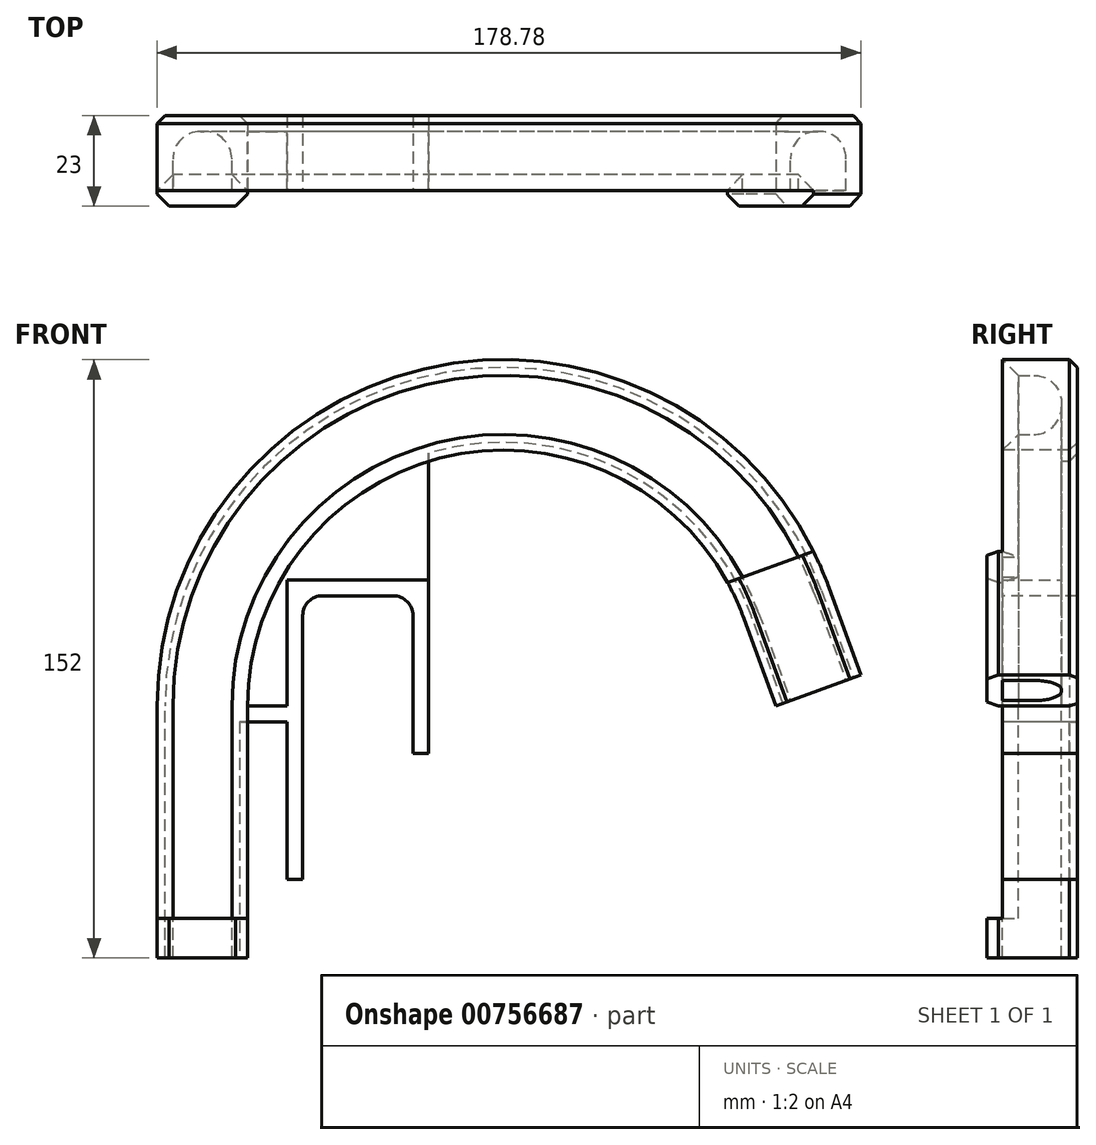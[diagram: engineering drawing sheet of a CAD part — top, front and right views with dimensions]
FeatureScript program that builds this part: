
annotation { "Feature Type Name" : "Feature", "Feature Type Description" : "" }
export const myFeature = defineFeature(function(context is Context, id is Id, definition is map)
    precondition{}
    {
        {
            var Q0;
            Q0=qCreatedBy(makeId("Front.planeOp"),FACE);
            var sketch = newSketch(context, id + "F0", { "sketchPlane" : qUnion([Q0])});
            skLineSegment(sketch, "E0.top", {"start": v(0, 60) * mm, "end": v(10, 60) * mm});
            skLineSegment(sketch, "E0.left", {"start": v(0, 0) * mm, "end": v(0, 60) * mm});
            skLineSegment(sketch, "E0.right", {"start": v(10, 20) * mm, "end": v(10, 60) * mm});
            skLineSegment(sketch, "E1.0", {"start": v(14, 20) * mm, "end": v(14, 64) * mm});
            skLineSegment(sketch, "E1.1", {"start": v(-4, 64) * mm, "end": v(14, 64) * mm});
            skLineSegment(sketch, "E1.2", {"start": v(-4, 0) * mm, "end": v(-4, 64) * mm});
            skLineSegment(sketch, "E2", {"start": v(10, 20) * mm, "end": v(14, 20) * mm});
            skLineSegment(sketch, "E3", {"start": v(-4, 0) * mm, "end": v(0, 0) * mm});
            skCircle(sketch, "E4", {"center": v(65, 64) * mm, "radius": 69 * mm, "construction": true});
            skLineSegment(sketch, "E5", {"start": v(65, 64) * mm, "end": v(129.84, 87.6) * mm, "construction": true});
            skArc(sketch, "E6", {"start": v(129.84, 87.6) * mm, "mid": v(53.02, 131.95) * mm, "end": v(-4, 64) * mm});
            skArc(sketch, "E7.0", {"start": v(126.08, 86.23) * mm, "mid": v(53.71, 128.01) * mm, "end": v(0, 64) * mm});
            skLineSegment(sketch, "E8", {"start": v(126.08, 86.23) * mm, "end": v(129.84, 87.6) * mm});
            skLineSegment(sketch, "E9.0", {"start": v(-19, 0) * mm, "end": v(-19, 64) * mm});
            skArc(sketch, "E9.1", {"start": v(143.93, 92.73) * mm, "mid": v(50.41, 146.72) * mm, "end": v(-19, 64) * mm});
            skLineSegment(sketch, "E10", {"start": v(-19, 0) * mm, "end": v(-4, 0) * mm});
            skLineSegment(sketch, "E11", {"start": v(143.93, 92.73) * mm, "end": v(129.84, 87.6) * mm});
            skLineSegment(sketch, "E12.0", {"start": v(-23, 0) * mm, "end": v(-23, 64) * mm});
            skArc(sketch, "E12.1", {"start": v(147.7, 94.1) * mm, "mid": v(49.72, 150.66) * mm, "end": v(-23, 64) * mm});
            skLineSegment(sketch, "E13", {"start": v(-23, 0) * mm, "end": v(-19, 0) * mm});
            skLineSegment(sketch, "E14", {"start": v(147.7, 94.1) * mm, "end": v(143.93, 92.73) * mm});
            skLineSegment(sketch, "E15", {"start": v(147.7, 94.1) * mm, "end": v(155.78, 71.87) * mm});
            skLineSegment(sketch, "E16", {"start": v(126.08, 86.23) * mm, "end": v(134.17, 64) * mm});
            skLineSegment(sketch, "E17", {"start": v(129.84, 87.6) * mm, "end": v(137.93, 65.37) * mm});
            skLineSegment(sketch, "E18", {"start": v(143.93, 92.73) * mm, "end": v(152.03, 70.5) * mm});
            skLineSegment(sketch, "E19", {"start": v(155.78, 71.87) * mm, "end": v(152.03, 70.5) * mm});
            skLineSegment(sketch, "E20", {"start": v(152.03, 70.5) * mm, "end": v(137.93, 65.37) * mm});
            skLineSegment(sketch, "E21", {"start": v(137.93, 65.37) * mm, "end": v(134.17, 64) * mm});
            skLineSegment(sketch, "E22", {"start": v(42, 52) * mm, "end": v(46, 52) * mm});
            skLineSegment(sketch, "E23", {"start": v(10, 64) * mm, "end": v(10, 92) * mm});
            skLineSegment(sketch, "E24", {"start": v(14, 92) * mm, "end": v(14, 64) * mm});
            skLineSegment(sketch, "E25", {"start": v(42, 92) * mm, "end": v(42, 52) * mm});
            skLineSegment(sketch, "E26", {"start": v(46, 52) * mm, "end": v(46, 92) * mm});
            skLineSegment(sketch, "E27", {"start": v(46, 92) * mm, "end": v(46, 128.01) * mm});
            skPoint(sketch, "E27.endSnap0", {"position": v(53.71, 128.01) * mm});
            skLineSegment(sketch, "E28", {"start": v(14, 92) * mm, "end": v(42, 92) * mm});
            skLineSegment(sketch, "E29", {"start": v(46, 96) * mm, "end": v(10, 96) * mm});
            skLineSegment(sketch, "E30", {"start": v(10, 96) * mm, "end": v(10, 92) * mm});
            skSolve(sketch);
        }
        {
            var Q0;
            Q0=qSketchRegion(id+"F0",true);
            extrude(context, id + "F1", {"entities" : qUnion([Q0]), "oppositeDirection" : true, "depth" : 4 * mm, "offsetDistance" : 25 * mm});
        }
        {
            var Q0;
            Q0=makeQuery(id+"F0.imprint","IMPRINT",FACE,{"disambiguationData":[TD([[makeQuery(id+"F0.imprint","IMPRINT",EDGE,{"derivedFrom":sQuery(id+"F0.wireOp",EDGE,"E0.top")}),1.0]])]});
            var Q1;
            {var subQ0=sQuery(id+"F0.wireOp",EDGE,"E6");Q1=makeQuery(id+"F0.imprint","IMPRINT",FACE,{"disambiguationData":[TD([[makeQuery(id+"F0.imprint","IMPRINT",EDGE,{"derivedFrom":subQ0}),1.0]])]});}
            var Q2;
            Q2=makeQuery(id+"F0.imprint","IMPRINT",FACE,{"disambiguationData":[TD([[makeQuery(id+"F0.imprint","IMPRINT",EDGE,{"derivedFrom":sQuery(id+"F0.wireOp",EDGE,"E9.0")}),1.0]])]});
            var Q3;
            Q3=makeQuery(id+"F0.imprint","IMPRINT",FACE,{"disambiguationData":[TD([[makeQuery(id+"F0.imprint","IMPRINT",EDGE,{"derivedFrom":sQuery(id+"F0.wireOp",EDGE,"E14")}),1.0]])]});
            var Q4;
            Q4=makeQuery(id+"F0.imprint","IMPRINT",FACE,{"disambiguationData":[TD([[makeQuery(id+"F0.imprint","IMPRINT",EDGE,{"derivedFrom":sQuery(id+"F0.wireOp",EDGE,"E8")}),-1.0]])]});
            var Q5;
            Q5=makeQuery(id+"F0.imprint","IMPRINT",FACE,{"disambiguationData":[TD([[makeQuery(id+"F0.imprint","IMPRINT",EDGE,{"derivedFrom":sQuery(id+"F0.wireOp",EDGE,"E22")}),1.0]])]});
            extrude(context, id + "F2", {"entities" : qUnion([Q0, Q1, Q2, Q3, Q4, Q5]), "operationType" : NewBodyOperationType.ADD, "depth" : 15 * mm, "offsetDistance" : 25 * mm});
        }
        {
            var Q0;
            Q0=makeQuery(id+"F2.opExtrude","CAP_EDGE",EDGE,{"disambiguationData":[OSD([sQuery(id+"F0.wireOp",EDGE,"E9.1")])],"isStart":true});
            var Q1;
            Q1=makeQuery(id+"F2.opExtrude","CAP_EDGE",EDGE,{"disambiguationData":[OSD([sQuery(id+"F0.wireOp",EDGE,"E6")])],"isStart":true});
            fillet(context, id + "F3", {"entities" : qUnion([Q0, Q1]), "radius" : 7 * mm, "tangentPropagation" : true, "allowEdgeOverflow" : false});
        }
        {
            var Q0;
            Q0=makeQuery(id+"F1.opExtrude","CAP_EDGE",EDGE,{"disambiguationData":[OSD([sQuery(id+"F0.wireOp",EDGE,"E16")])],"isStart":false});
            var Q1;
            Q1=makeQuery(id+"F1.opExtrude","CAP_EDGE",EDGE,{"disambiguationData":[OSD([sQuery(id+"F0.wireOp",EDGE,"E15")])],"isStart":false});
            var Q2;
            Q2=makeQuery(id+"F1.opExtrude","CAP_EDGE",EDGE,{"disambiguationData":[OSD([sQuery(id+"F0.wireOp",EDGE,"E0.left")])],"isStart":false});
            chamfer(context, id + "F4", {"entities" : qUnion([Q0, Q1, Q2]), "width" : 2 * mm, "tangentPropagation" : true});
        }
        {
            var Q0;
            Q0=makeQuery(id+"F2.opExtrude","CAP_FACE",FACE,{"disambiguationData":[OSD([sQuery(id+"F0.wireOp",EDGE,"E0.top"),sQuery(id+"F0.wireOp",EDGE,"E0.left"),sQuery(id+"F0.wireOp",EDGE,"E0.right"),sQuery(id+"F0.wireOp",EDGE,"E1.0"),sQuery(id+"F0.wireOp",EDGE,"E1.1"),sQuery(id+"F0.wireOp",EDGE,"E1.2"),sQuery(id+"F0.wireOp",EDGE,"E2"),sQuery(id+"F0.wireOp",EDGE,"E3"),sQuery(id+"F0.wireOp",EDGE,"E6"),sQuery(id+"F0.wireOp",EDGE,"E7.0"),sQuery(id+"F0.wireOp",EDGE,"E8")])],"isStart":false});
            var sketch = newSketch(context, id + "F5", { "sketchPlane" : qUnion([Q0])});
            skLineSegment(sketch, "E31.bottom", {"start": v(0, 0) * mm, "end": v(-23, 0) * mm});
            skLineSegment(sketch, "E31.top", {"start": v(0, 10) * mm, "end": v(-23, 10) * mm});
            skLineSegment(sketch, "E31.left", {"start": v(0, 0) * mm, "end": v(0, 10) * mm});
            skLineSegment(sketch, "E31.right", {"start": v(-23, 0) * mm, "end": v(-23, 10) * mm});
            skLineSegment(sketch, "E32", {"start": v(126.08, 86.23) * mm, "end": v(147.7, 94.1) * mm});
            skLineSegment(sketch, "E33", {"start": v(1.23, 51.43) * mm, "end": v(143.74, 103.3) * mm});
            skArc(sketch, "E34", {"start": v(126.08, 86.23) * mm, "mid": v(47.55, 126.61) * mm, "end": v(1.23, 51.43) * mm});
            skArc(sketch, "E35", {"start": v(147.7, 94.1) * mm, "mid": v(145.85, 98.76) * mm, "end": v(143.74, 103.3) * mm});
            skLineSegment(sketch, "E36", {"start": v(126.08, 86.23) * mm, "end": v(134.17, 64) * mm});
            skLineSegment(sketch, "E37", {"start": v(134.17, 64) * mm, "end": v(155.78, 71.87) * mm});
            skLineSegment(sketch, "E38", {"start": v(155.78, 71.87) * mm, "end": v(147.7, 94.1) * mm});
            skSolve(sketch);
        }
        {
            var Q0;
            {var subQ2=sQuery(id+"F5.wireOp",EDGE,"E36");Q0=makeQuery(id+"F5.imprint","IMPRINT",FACE,{"disambiguationData":[TD([[makeQuery(id+"F5.imprint","IMPRINT",EDGE,{"derivedFrom":subQ2}),1.0]])]});}
            var Q1;
            {var subQ2=sQuery(id+"F5.wireOp",EDGE,"E38");Q1=makeQuery(id+"F5.imprint","IMPRINT",FACE,{"disambiguationData":[TD([[makeQuery(id+"F5.imprint","IMPRINT",EDGE,{"derivedFrom":subQ2}),1.0]])]});}
            var Q2;
            {var subQ3=sQuery(id+"F5.wireOp",EDGE,"E31.right");Q2=makeQuery(id+"F5.imprint","IMPRINT",FACE,{"disambiguationData":[TD([[makeQuery(id+"F5.imprint","IMPRINT",EDGE,{"derivedFrom":subQ3}),-1.0]])]});}
            var Q3;
            {var subQ0=sQuery(id+"F5.wireOp",EDGE,"E31.left");Q3=makeQuery(id+"F5.imprint","IMPRINT",FACE,{"disambiguationData":[TD([[makeQuery(id+"F5.imprint","IMPRINT",EDGE,{"derivedFrom":subQ0}),1.0]])]});}
            var Q4;
            {var subQ3=sQuery(id+"F5.wireOp",EDGE,"E35");Q4=makeQuery(id+"F5.imprint","IMPRINT",FACE,{"disambiguationData":[TD([[makeQuery(id+"F5.imprint","IMPRINT",EDGE,{"derivedFrom":subQ3}),1.0]])]});}
            var Q5;
            {var subQ3=sQuery(id+"F5.wireOp",EDGE,"E34");var subQ5=sQuery(id+"F5.wireOp",EDGE,"E33");var subQ6=makeQuery(id+"F5.imprint","INTERSECT",VERTEX,{"disambiguationData":[OD(1.0)],"derivedFrom":[subQ5,subQ3]});Q5=makeQuery(id+"F5.imprint","IMPRINT",FACE,{"disambiguationData":[TD([[makeQuery(id+"F5.imprint","IMPRINT",EDGE,{"disambiguationData":[TD([[subQ6,-1.0]])],"derivedFrom":subQ5}),-1.0]])]});}
            extrude(context, id + "F6", {"entities" : qUnion([Q0, Q1, Q2, Q3, Q4, Q5]), "operationType" : NewBodyOperationType.ADD, "depth" : 4 * mm, "offsetDistance" : 25 * mm});
        }
        {
            var Q0;
            {var subQ0=sQuery(id+"F0.wireOp",EDGE,"E9.0");Q0=makeQuery(id+"F6.boolean.opBoolean","SPLIT",EDGE,{"disambiguationData":[topologyDisambiguationEdgeConnected([makeQuery(id+"F6.opExtrude","CAP_FACE",FACE,{"disambiguationData":[OSD([sQuery(id+"F5.wireOp",EDGE,"E31.bottom"),sQuery(id+"F5.wireOp",EDGE,"E31.top"),sQuery(id+"F5.wireOp",EDGE,"E31.left"),sQuery(id+"F5.wireOp",EDGE,"E31.right")])],"isStart":true})])],"derivedFrom":makeQuery(id+"F2.opExtrude","CAP_EDGE",EDGE,{"disambiguationData":[OSD([subQ0])],"isStart":false})});}
            var Q1;
            {var subQ0=sQuery(id+"F0.wireOp",EDGE,"E1.2");Q1=makeQuery(id+"F6.boolean.opBoolean","SPLIT",EDGE,{"disambiguationData":[topologyDisambiguationEdgeConnected([makeQuery(id+"F6.opExtrude","CAP_FACE",FACE,{"disambiguationData":[OSD([sQuery(id+"F5.wireOp",EDGE,"E31.bottom"),sQuery(id+"F5.wireOp",EDGE,"E31.top"),sQuery(id+"F5.wireOp",EDGE,"E31.left"),sQuery(id+"F5.wireOp",EDGE,"E31.right")])],"isStart":true})])],"derivedFrom":makeQuery(id+"F2.opExtrude","CAP_EDGE",EDGE,{"disambiguationData":[OSD([subQ0])],"isStart":false})});}
            var Q2;
            {var subQ0=sQuery(id+"F0.wireOp",EDGE,"E9.1");Q2=makeQuery(id+"F6.boolean.opBoolean","SPLIT",EDGE,{"disambiguationData":[topologyDisambiguationEdgeConnected([makeQuery(id+"F6.opExtrude","CAP_FACE",FACE,{"disambiguationData":[OSD([sQuery(id+"F5.wireOp",EDGE,"E32"),sQuery(id+"F5.wireOp",EDGE,"E33"),sQuery(id+"F5.wireOp",EDGE,"E34"),sQuery(id+"F5.wireOp",EDGE,"E35")])],"isStart":true})])],"derivedFrom":makeQuery(id+"F2.opExtrude","CAP_EDGE",EDGE,{"disambiguationData":[OSD([subQ0])],"isStart":false})});}
            var Q3;
            {var subQ0=sQuery(id+"F0.wireOp",EDGE,"E6");Q3=makeQuery(id+"F6.boolean.opBoolean","SPLIT",EDGE,{"disambiguationData":[topologyDisambiguationEdgeConnected([makeQuery(id+"F6.opExtrude","CAP_FACE",FACE,{"disambiguationData":[OSD([sQuery(id+"F5.wireOp",EDGE,"E32"),sQuery(id+"F5.wireOp",EDGE,"E33"),sQuery(id+"F5.wireOp",EDGE,"E34"),sQuery(id+"F5.wireOp",EDGE,"E35")])],"isStart":true})])],"derivedFrom":makeQuery(id+"F2.opExtrude","CAP_EDGE",EDGE,{"disambiguationData":[OSD([subQ0])],"isStart":false})});}
            chamfer(context, id + "F7", {"entities" : qUnion([Q0, Q1, Q2, Q3]), "width" : 4 * mm, "tangentPropagation" : true});
        }
        {
            var Q0;
            Q0=makeQuery(id+"F6.opExtrude","CAP_EDGE",EDGE,{"disambiguationData":[OSD([sQuery(id+"F5.wireOp",EDGE,"E31.right")])],"isStart":false});
            var Q1;
            Q1=makeQuery(id+"F6.opExtrude","CAP_EDGE",EDGE,{"disambiguationData":[OSD([sQuery(id+"F5.wireOp",EDGE,"E31.left")])],"isStart":false});
            var Q2;
            Q2=makeQuery(id+"F6.opExtrude","CAP_EDGE",EDGE,{"disambiguationData":[OSD([sQuery(id+"F5.wireOp",EDGE,"E34")])],"isStart":false});
            var Q3;
            Q3=makeQuery(id+"F6.opExtrude","CAP_EDGE",EDGE,{"disambiguationData":[OSD([sQuery(id+"F5.wireOp",EDGE,"E35")])],"isStart":false});
            chamfer(context, id + "F8", {"entities" : qUnion([Q0, Q1, Q2, Q3]), "width" : 3 * mm, "tangentPropagation" : true});
        }
        {
            var Q0;
            {var subQ0=sQuery(id+"F0.wireOp",EDGE,"E28");var subQ1=sQuery(id+"F0.wireOp",EDGE,"E25");Q0=makeQuery(id+"F2.boolean.opBoolean","MERGE",EDGE,{"derivedFrom":[makeQuery(id+"F1.opExtrude","SWEPT_EDGE",EDGE,{"disambiguationData":[OSD([subQ1,subQ0])]}),makeQuery(id+"F2.opExtrude","SWEPT_EDGE",EDGE,{"disambiguationData":[OSD([subQ1,subQ0])]})]});}
            var Q1;
            {var subQ0=sQuery(id+"F0.wireOp",EDGE,"E28");var subQ1=sQuery(id+"F0.wireOp",EDGE,"E24");Q1=makeQuery(id+"F2.boolean.opBoolean","MERGE",EDGE,{"derivedFrom":[makeQuery(id+"F1.opExtrude","SWEPT_EDGE",EDGE,{"disambiguationData":[OSD([subQ1,subQ0])]}),makeQuery(id+"F2.opExtrude","SWEPT_EDGE",EDGE,{"disambiguationData":[OSD([subQ1,subQ0])]})]});}
            fillet(context, id + "F9", {"entities" : qUnion([Q0, Q1]), "radius" : 5 * mm, "tangentPropagation" : true, "allowEdgeOverflow" : false});
        }
    });
